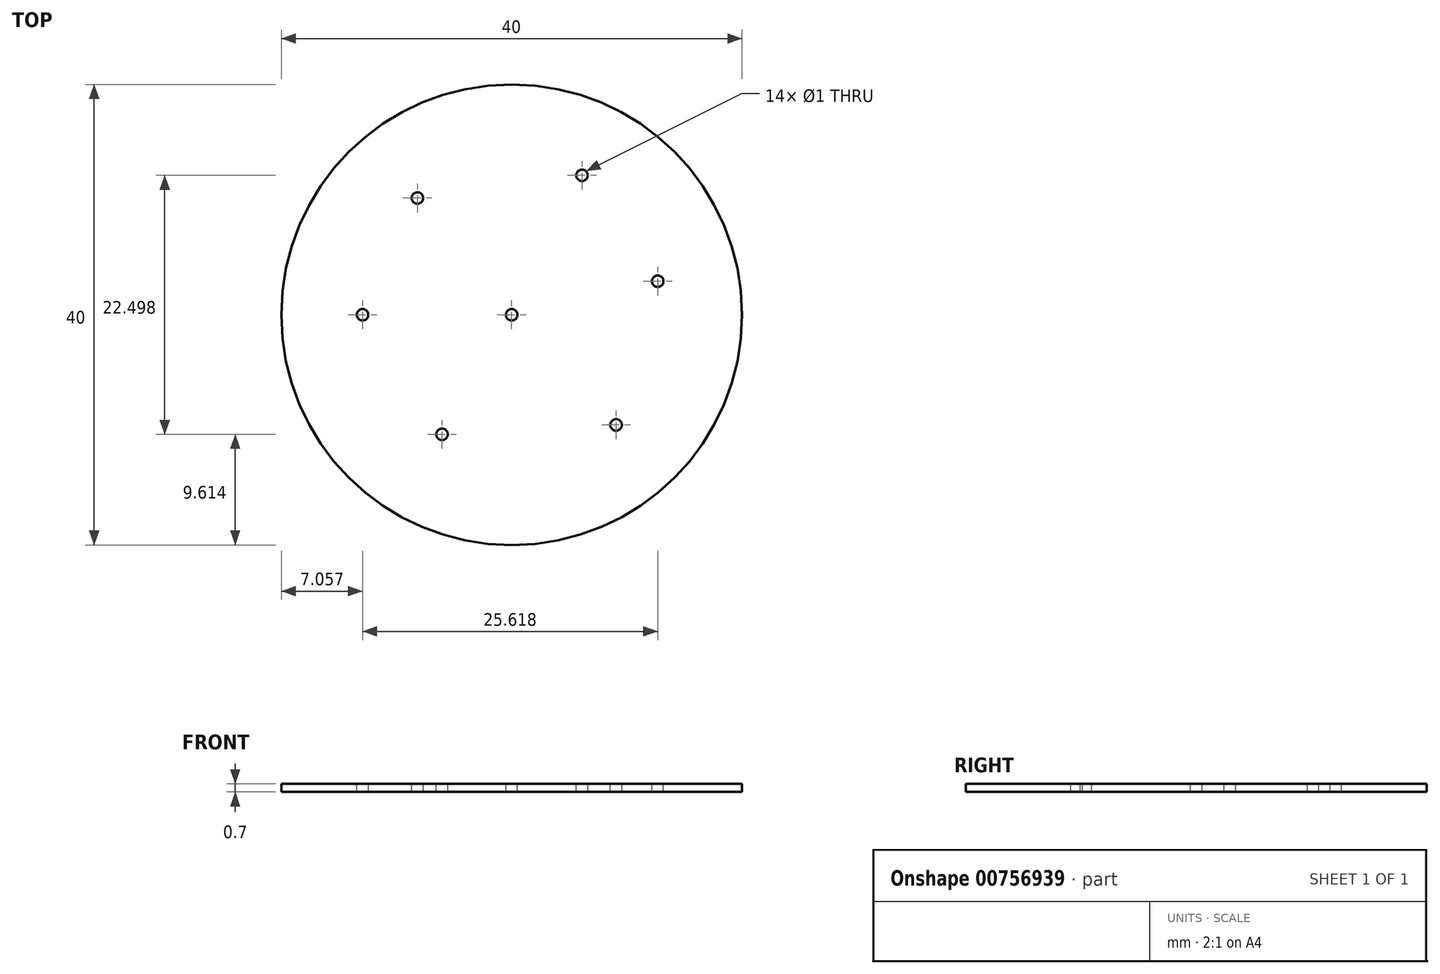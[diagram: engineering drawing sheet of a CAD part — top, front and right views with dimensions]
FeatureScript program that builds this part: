
annotation { "Feature Type Name" : "Feature", "Feature Type Description" : "" }
export const myFeature = defineFeature(function(context is Context, id is Id, definition is map)
    precondition{}
    {
        {
            var Q0;
            Q0=qCreatedBy(makeId("Top.planeOp"),FACE);
            var sketch = newSketch(context, id + "F0", { "sketchPlane" : qUnion([Q0])});
            skCircle(sketch, "E0", {"center": v(0, 0) * mm, "radius": 20 * mm});
            skSolve(sketch);
        }
        {
            var Q0;
            Q0=qSketchRegion(id+"F0",true);
            extrude(context, id + "F1", {"entities" : qUnion([Q0]), "depth" : 0.7 * mm, "offsetDistance" : 25 * mm});
        }
        {
            var Q0;
            Q0=makeQuery(id+"F1.opExtrude","CAP_FACE",FACE,{"disambiguationData":[OSD([sQuery(id+"F0.wireOp",EDGE,"E0")])],"isStart":false});
            var sketch = newSketch(context, id + "F2", { "sketchPlane" : qUnion([Q0])});
            skCircle(sketch, "E1", {"center": v(-12.94, 0) * mm, "radius": 0.5 * mm});
            skCircle(sketch, "E2", {"center": v(12.68, 2.92) * mm, "radius": 0.5 * mm});
            skCircle(sketch, "E3", {"center": v(9.06, -9.57) * mm, "radius": 0.5 * mm});
            skCircle(sketch, "E4", {"center": v(0, 0) * mm, "radius": 0.5 * mm});
            skCircle(sketch, "E5", {"center": v(-8.18, 10.14) * mm, "radius": 0.5 * mm});
            skCircle(sketch, "E6", {"center": v(-6.05, -10.39) * mm, "radius": 0.5 * mm});
            skCircle(sketch, "E7", {"center": v(6.1, 12.11) * mm, "radius": 0.5 * mm});
            skSolve(sketch);
        }
        {
            var Q0;
            Q0=qSketchRegion(id+"F2",true);
            extrude(context, id + "F3", {"entities" : qUnion([Q0]), "operationType" : NewBodyOperationType.REMOVE, "oppositeDirection" : true, "depth" : 0.7 * mm, "offsetDistance" : 25 * mm});
        }
    });
